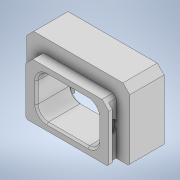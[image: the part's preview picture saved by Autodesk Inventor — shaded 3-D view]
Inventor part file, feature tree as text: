
AUTODESK INVENTOR PART (.ipt)
format: ipt  version: 2020.2 (Build 242310000, 310)  size: 296,448 bytes
history: native  units: mm
features: extrude x7, sketch x7, projected_geometry x3, fillet x2, chamfer x2, mirror x1
ambient origin geometry x8: Origin, YZ Plane, XZ Plane, XY Plane, X Axis, Y Axis, Z Axis, Center Point
bodies: Solid1 (feature_tree)
feature tree (22):
  extrude  "Extrusion1"  Depth=20.0mm
  extrude  "Extrusion2"  Depth=12.0mm
  extrude  "Extrusion3"  Depth=22.0mm
  extrude  "Extrusion4"  Depth=2.2mm TaperAngle=0.0deg
  extrude  "Extrusion5"  Depth=1.0mm TaperAngle=0.0deg
  extrude  "Extrusion6"  Depth=0.6mm TaperAngle=0.0deg
  fillet  "Fillet3"  Radius=6.8mm
  fillet  "Fillet1"  Radius=1.5mm
  mirror  "Mirror1"
  chamfer  "Chamfer1"  Distance=16.0mm
  chamfer  "Chamfer2"  Distance=3.0mm
  extrude  "Extrusion7"  Depth=22.0mm
  sketch  "Sketch1"  dims[d0=30.0mm d1=20.0mm]
  sketch  "Sketch2"  dims[d2=18.0mm d3=12.0mm]
  projected_geometry  "Projected Loop1"
  sketch  "Sketch3"  dims[d4=7.0mm d5=0.0mm d6=22.0mm]
  sketch  "Sketch4"  dims[d7=16.0mm d8=2.2mm d9=0.0mm]
  projected_geometry  "Projected Loop2"
  sketch  "Sketch5"  dims[d10=24.2mm d11=1.0mm d12=0.0mm]
  projected_geometry  "Projected Loop3"
  sketch  "Sketch6"  dims[d13=2.0mm d17=0.6mm d18=0.0mm d19=6.8mm d20=1.5mm]
  sketch  "Sketch8"  dims[d21=25.0mm d22=16.0mm d23=3.0mm d24=0.0mm d26=22.0mm d27=11.0mm d28=21.6mm d29=10.8mm d30=45.0deg d31=45.0deg d32=45.0deg d33=45.0deg d34=7.5mm d35=2.0mm d36=1.4mm d37=0.0mm d38=3.0mm d40=2.0mm d41=2.0mm d42=2.0mm d43=45.0deg d44=0.5mm d45=2.0mm d46=45.0deg d47=10.0mm d48=0.0mm]
